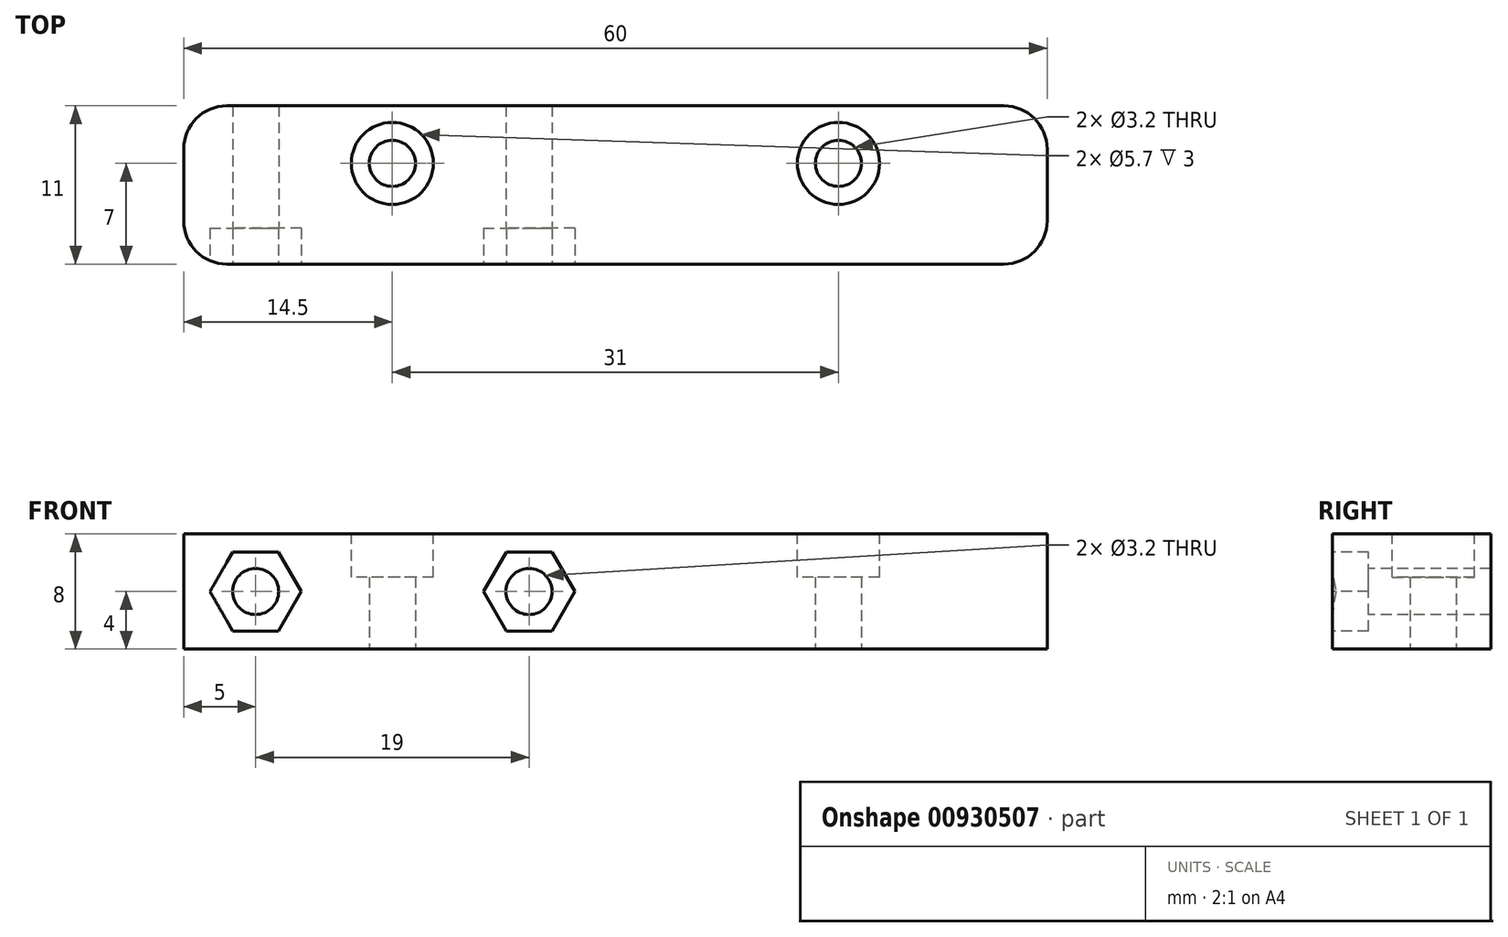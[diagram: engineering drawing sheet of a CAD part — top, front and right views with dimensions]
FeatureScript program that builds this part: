
annotation { "Feature Type Name" : "Feature", "Feature Type Description" : "" }
export const myFeature = defineFeature(function(context is Context, id is Id, definition is map)
    precondition{}
    {
        {
            assignVariable(context, id + "F0", {"name" : "Tolerance", "anyValue" : 0.2});
        }
        {
            var Q0;
            Q0=qCreatedBy(makeId("Top.planeOp"),FACE);
            var sketch = newSketch(context, id + "F1", { "sketchPlane" : qUnion([Q0])});
            skPoint(sketch, "E0", {"position": v(0, 0) * mm});
            skPoint(sketch, "E1", {"position": v(31, 0) * mm});
            skCircle(sketch, "E2", {"center": v(0, 0) * mm, "radius": 1.6 * mm});
            skCircle(sketch, "E3", {"center": v(31, 0) * mm, "radius": 1.6 * mm});
            skPoint(sketch, "E4", {"position": v(45.5, 0) * mm});
            skPoint(sketch, "E5", {"position": v(-14.5, 0) * mm});
            skLineSegment(sketch, "E6", {"start": v(45.5, 0) * mm, "end": v(45.5, 4) * mm});
            skLineSegment(sketch, "E7", {"start": v(-14.5, 0) * mm, "end": v(-14.5, -0.2) * mm});
            skLineSegment(sketch, "E8", {"start": v(-14.5, 0) * mm, "end": v(-14.5, 4) * mm});
            skLineSegment(sketch, "E9", {"start": v(-9.5, -7) * mm, "end": v(40.5, -7) * mm});
            skLineSegment(sketch, "E10", {"start": v(45.5, 4) * mm, "end": v(-14.5, 4) * mm});
            skLineSegment(sketch, "E11", {"start": v(-9.5, -7) * mm, "end": v(-9.5, -7) * mm});
            skPoint(sketch, "E12.visualSharp", {"position": v(-14.5, -7) * mm});
            skLineSegment(sketch, "E13", {"start": v(-14.5, 0) * mm, "end": v(-14.5, -7) * mm});
            skLineSegment(sketch, "E14", {"start": v(-9.5, -7) * mm, "end": v(-14.5, -7) * mm});
            skLineSegment(sketch, "E15", {"start": v(45.5, 0) * mm, "end": v(45.5, -7) * mm});
            skLineSegment(sketch, "E16", {"start": v(45.5, -7) * mm, "end": v(40.5, -7) * mm});
            skSolve(sketch);
        }
        {
            var Q0;
            Q0 = qSketchRegion(id + "F1", true);
            extrude(context, id + "F2", {"entities" : qUnion([Q0]), "depth" : 8 * mm, "offsetDistance" : 25 * mm});
        }
        {
            var Q0;
            Q0=makeQuery(id+"F2.opExtrude","CAP_FACE",FACE,{"disambiguationData":[OSD([sQuery(id+"F1.wireOp",EDGE,"E2"),sQuery(id+"F1.wireOp",EDGE,"E3"),sQuery(id+"F1.wireOp",EDGE,"HMMrT8qh-GEIL-QASa-77MW-rDlcdwNgUnP6"),sQuery(id+"F1.wireOp",EDGE,"E6"),sQuery(id+"F1.wireOp",EDGE,"E7"),sQuery(id+"F1.wireOp",EDGE,"E8"),sQuery(id+"F1.wireOp",EDGE,"E9"),sQuery(id+"F1.wireOp",EDGE,"E10"),sQuery(id+"F1.wireOp",EDGE,"532e6abd-660c-4c3c-83fc-3c3830de58d2.filletArc"),sQuery(id+"F1.wireOp",EDGE,"f1bde773-ca21-4f97-be8d-ab0e7ffa0f7f.filletArc")])],"isStart":false});
            var sketch = newSketch(context, id + "F3", { "sketchPlane" : qUnion([Q0])});
            skCircle(sketch, "E17", {"center": v(0, 0) * mm, "radius": 2.85 * mm});
            skCircle(sketch, "E18", {"center": v(31, 0) * mm, "radius": 2.85 * mm});
            skSolve(sketch);
        }
        {
            var Q0;
            Q0 = qSketchRegion(id + "F3", true);
            extrude(context, id + "F4", {"entities" : qUnion([Q0]), "operationType" : NewBodyOperationType.REMOVE, "oppositeDirection" : true, "depth" : 3 * mm, "offsetDistance" : 25 * mm});
        }
        {
            var Q0;
            Q0=makeQuery(id+"F2.opExtrude","SWEPT_FACE",FACE,{"disambiguationData":[OSD([sQuery(id+"F1.wireOp",EDGE,"E9"),sQuery(id+"F1.wireOp",EDGE,"E11")])]});
            var sketch = newSketch(context, id + "F5", { "sketchPlane" : qUnion([Q0])});
            skCircle(sketch, "E19.cCircle", {"center": v(-9.5, 4) * mm, "radius": 2.75 * mm, "construction": true});
            skPoint(sketch, "E19.cCircle.centerSnap0", {"position": v(-14.5, 4) * mm});
            skLineSegment(sketch, "E19.0", {"start": v(-11.09, 6.75) * mm, "end": v(-7.91, 6.75) * mm});
            skLineSegment(sketch, "E19.1", {"start": v(-7.91, 6.75) * mm, "end": v(-6.32, 4) * mm});
            skLineSegment(sketch, "E19.2", {"start": v(-6.32, 4) * mm, "end": v(-7.91, 1.25) * mm});
            skLineSegment(sketch, "E19.3", {"start": v(-7.91, 1.25) * mm, "end": v(-11.09, 1.25) * mm});
            skLineSegment(sketch, "E19.4", {"start": v(-11.09, 1.25) * mm, "end": v(-12.68, 4) * mm});
            skLineSegment(sketch, "E19.5", {"start": v(-12.68, 4) * mm, "end": v(-11.09, 6.75) * mm});
            skPoint(sketch, "E19.0.midPoint", {"position": v(-9.5, 6.75) * mm});
            skCircle(sketch, "E20.cCircle", {"center": v(9.5, 4) * mm, "radius": 2.75 * mm, "construction": true});
            skLineSegment(sketch, "E20.0", {"start": v(7.91, 6.75) * mm, "end": v(11.09, 6.75) * mm});
            skLineSegment(sketch, "E20.1", {"start": v(11.09, 6.75) * mm, "end": v(12.68, 4) * mm});
            skLineSegment(sketch, "E20.2", {"start": v(12.68, 4) * mm, "end": v(11.09, 1.25) * mm});
            skLineSegment(sketch, "E20.3", {"start": v(11.09, 1.25) * mm, "end": v(7.91, 1.25) * mm});
            skLineSegment(sketch, "E20.4", {"start": v(7.91, 1.25) * mm, "end": v(6.32, 4) * mm});
            skLineSegment(sketch, "E20.5", {"start": v(6.32, 4) * mm, "end": v(7.91, 6.75) * mm});
            skPoint(sketch, "E20.0.midPoint", {"position": v(9.5, 6.75) * mm});
            skSolve(sketch);
        }
        {
            var Q0;
            Q0 = qSketchRegion(id + "F5", true);
            extrude(context, id + "F6", {"entities" : qUnion([Q0]), "operationType" : NewBodyOperationType.REMOVE, "oppositeDirection" : true, "depth" : 2.5 * mm, "offsetDistance" : 25 * mm});
        }
        {
            var Q0;
            Q0=sQuery(id+"F5.wireOp",VERTEX,"E19.cCircle.center");
            var Q1;
            Q1=sQuery(id+"F5.wireOp",VERTEX,"E20.cCircle.center");
            var Q2;
            Q2=makeQuery(id+"F2.opExtrude","SWEPT_BODY",BODY,{"disambiguationData":[OSD([sQuery(id+"F1.wireOp",EDGE,"E2"),sQuery(id+"F1.wireOp",EDGE,"E3"),sQuery(id+"F1.wireOp",EDGE,"HMMrT8qh-GEIL-QASa-77MW-rDlcdwNgUnP6"),sQuery(id+"F1.wireOp",EDGE,"E6"),sQuery(id+"F1.wireOp",EDGE,"E7"),sQuery(id+"F1.wireOp",EDGE,"E8"),sQuery(id+"F1.wireOp",EDGE,"E9"),sQuery(id+"F1.wireOp",EDGE,"E10"),sQuery(id+"F1.wireOp",EDGE,"532e6abd-660c-4c3c-83fc-3c3830de58d2.filletArc"),sQuery(id+"F1.wireOp",EDGE,"E11"),sQuery(id+"F1.wireOp",EDGE,"iBlgqElS-F0GE-TYZS-sko4-dzfef5jipdni")])]});
            hole(context, id + "F7", {"style" : HoleStyle.SIMPLE, "endStyle" : HoleEndStyle.THROUGH, "holeDiameter" : (3 + getVariable(context, 'Tolerance')) * mm, "majorDiameter" : 5 * mm, "isTappedThrough" : true, "tappedDepth" : 12 * mm, "tapClearance" : 3, "locations" : qUnion([Q0, Q1]), "scope" : qUnion([Q2])});
        }
        {
            var Q0;
            Q0=makeQuery(id+"F2.opExtrude","SWEPT_EDGE",EDGE,{"disambiguationData":[OSD([sQuery(id+"F1.wireOp",EDGE,"E8"),sQuery(id+"F1.wireOp",EDGE,"E10")])]});
            var Q1;
            Q1=makeQuery(id+"F2.opExtrude","SWEPT_EDGE",EDGE,{"disambiguationData":[OSD([sQuery(id+"F1.wireOp",EDGE,"E15"),sQuery(id+"F1.wireOp",EDGE,"E16")])]});
            var Q2;
            Q2=makeQuery(id+"F2.opExtrude","SWEPT_EDGE",EDGE,{"disambiguationData":[OSD([sQuery(id+"F1.wireOp",EDGE,"E6"),sQuery(id+"F1.wireOp",EDGE,"E10")])]});
            var Q3;
            Q3=makeQuery(id+"F2.opExtrude","SWEPT_EDGE",EDGE,{"disambiguationData":[OSD([sQuery(id+"F1.wireOp",EDGE,"E13"),sQuery(id+"F1.wireOp",EDGE,"E14")])]});
            fillet(context, id + "F8", {"entities" : qUnion([Q0, Q1, Q2, Q3]), "radius" : 3 * mm, "tangentPropagation" : true, "allowEdgeOverflow" : false});
        }
    });
